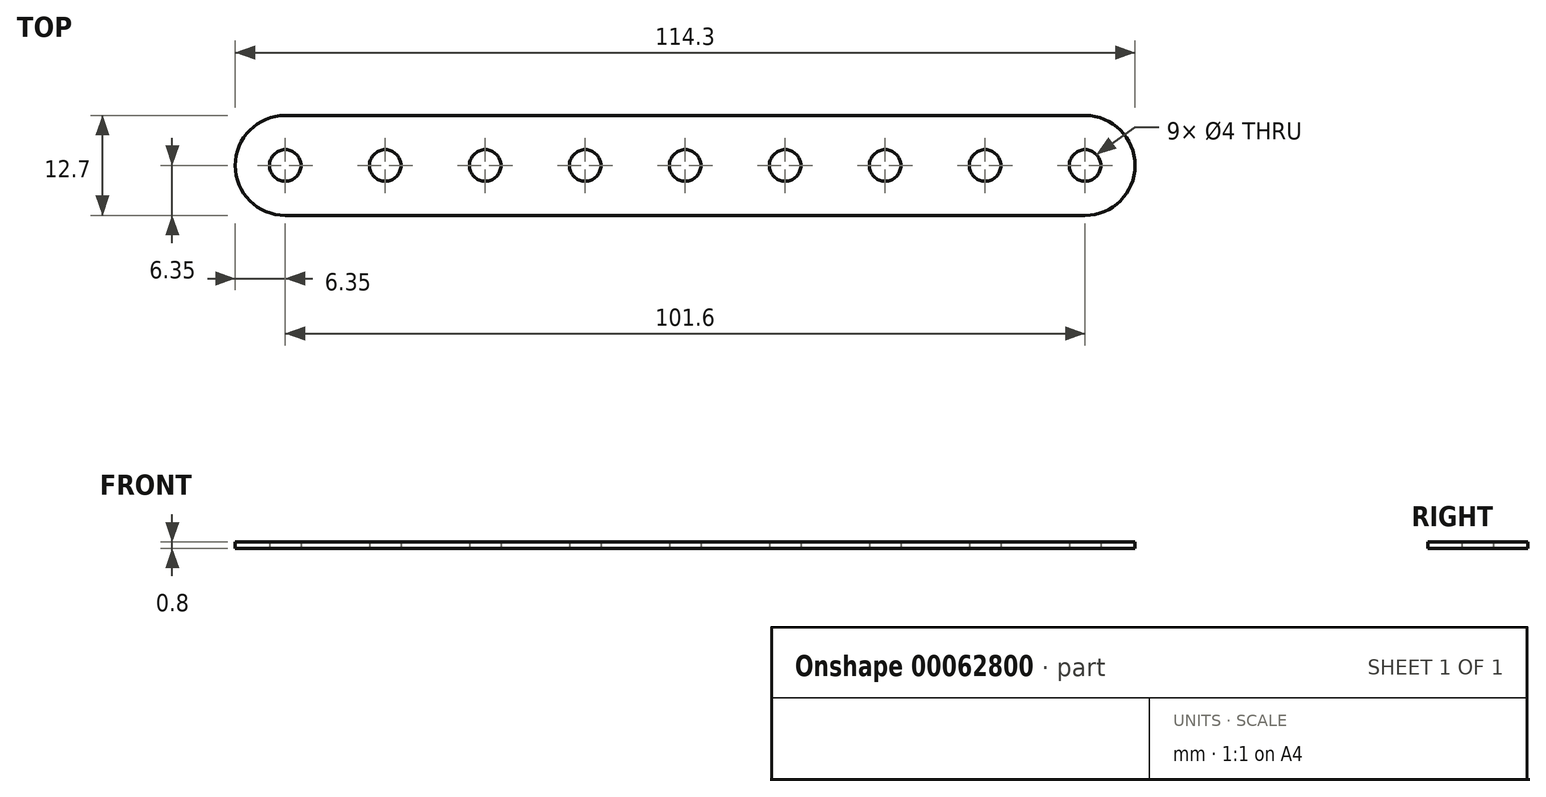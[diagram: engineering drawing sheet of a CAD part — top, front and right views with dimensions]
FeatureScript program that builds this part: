
annotation { "Feature Type Name" : "Feature", "Feature Type Description" : "" }
export const myFeature = defineFeature(function(context is Context, id is Id, definition is map)
    precondition{}
    {
        {
            var Q0;
            Q0=qCreatedBy(makeId("Top.planeOp"),FACE);
            var sketch = newSketch(context, id + "F0", { "sketchPlane" : qUnion([Q0])});
            skCircle(sketch, "E0", {"center": v(0, 0) * mm, "radius": 2 * mm});
            skCircle(sketch, "E1.1.0.0", {"center": v(12.7, 0) * mm, "radius": 2 * mm});
            skCircle(sketch, "E1.2.0.0", {"center": v(25.4, 0) * mm, "radius": 2 * mm});
            skCircle(sketch, "E1.3.0.0", {"center": v(38.1, 0) * mm, "radius": 2 * mm});
            skCircle(sketch, "E1.4.0.0", {"center": v(50.8, 0) * mm, "radius": 2 * mm});
            skCircle(sketch, "E1.5.0.0", {"center": v(63.5, 0) * mm, "radius": 2 * mm});
            skCircle(sketch, "E1.6.0.0", {"center": v(76.2, 0) * mm, "radius": 2 * mm});
            skCircle(sketch, "E1.7.0.0", {"center": v(88.9, 0) * mm, "radius": 2 * mm});
            skCircle(sketch, "E1.8.0.0", {"center": v(101.6, 0) * mm, "radius": 2 * mm});
            skLineSegment(sketch, "E1.direction1", {"start": v(0, 0) * mm, "end": v(12.7, 0) * mm, "construction": true});
            skLineSegment(sketch, "E2.rect.bottom", {"start": v(101.6, -6.35) * mm, "end": v(0, -6.35) * mm});
            skLineSegment(sketch, "E2.rect.top", {"start": v(101.6, 6.35) * mm, "end": v(0, 6.35) * mm});
            skLineSegment(sketch, "E2.rect.left", {"start": v(107.95, 0) * mm, "end": v(107.95, 0) * mm});
            skLineSegment(sketch, "E2.rect.right", {"start": v(-6.35, 0) * mm, "end": v(-6.35, 0) * mm});
            skPoint(sketch, "E3.visualSharp", {"position": v(-6.35, 6.35) * mm});
            skArc(sketch, "E3.filletArc", {"start": v(0, 6.35) * mm, "mid": v(-4.5, 4.5) * mm, "end": v(-6.35, 0) * mm});
            skPoint(sketch, "E4.visualSharp", {"position": v(-6.35, -6.35) * mm});
            skArc(sketch, "E4.filletArc", {"start": v(-6.35, 0) * mm, "mid": v(-4.5, -4.5) * mm, "end": v(0, -6.35) * mm});
            skPoint(sketch, "E5.visualSharp", {"position": v(107.95, 6.35) * mm});
            skArc(sketch, "E5.filletArc", {"start": v(107.95, 0) * mm, "mid": v(106.1, 4.5) * mm, "end": v(101.6, 6.35) * mm});
            skPoint(sketch, "E6.visualSharp", {"position": v(107.95, -6.35) * mm});
            skArc(sketch, "E6.filletArc", {"start": v(101.6, -6.35) * mm, "mid": v(106.1, -4.5) * mm, "end": v(107.95, 0) * mm});
            skSolve(sketch);
        }
        {
            var Q0;
            Q0=makeQuery(id+"F0.imprint","IMPRINT",FACE,{"disambiguationData":[TD([[makeQuery(id+"F0.imprint","IMPRINT",EDGE,{"derivedFrom":sQuery(id+"F0.wireOp",EDGE,"E0")}),-1.0]])]});
            extrude(context, id + "F1", {"entities" : qUnion([Q0]), "depth" : 0.8 * mm});
        }
    });
